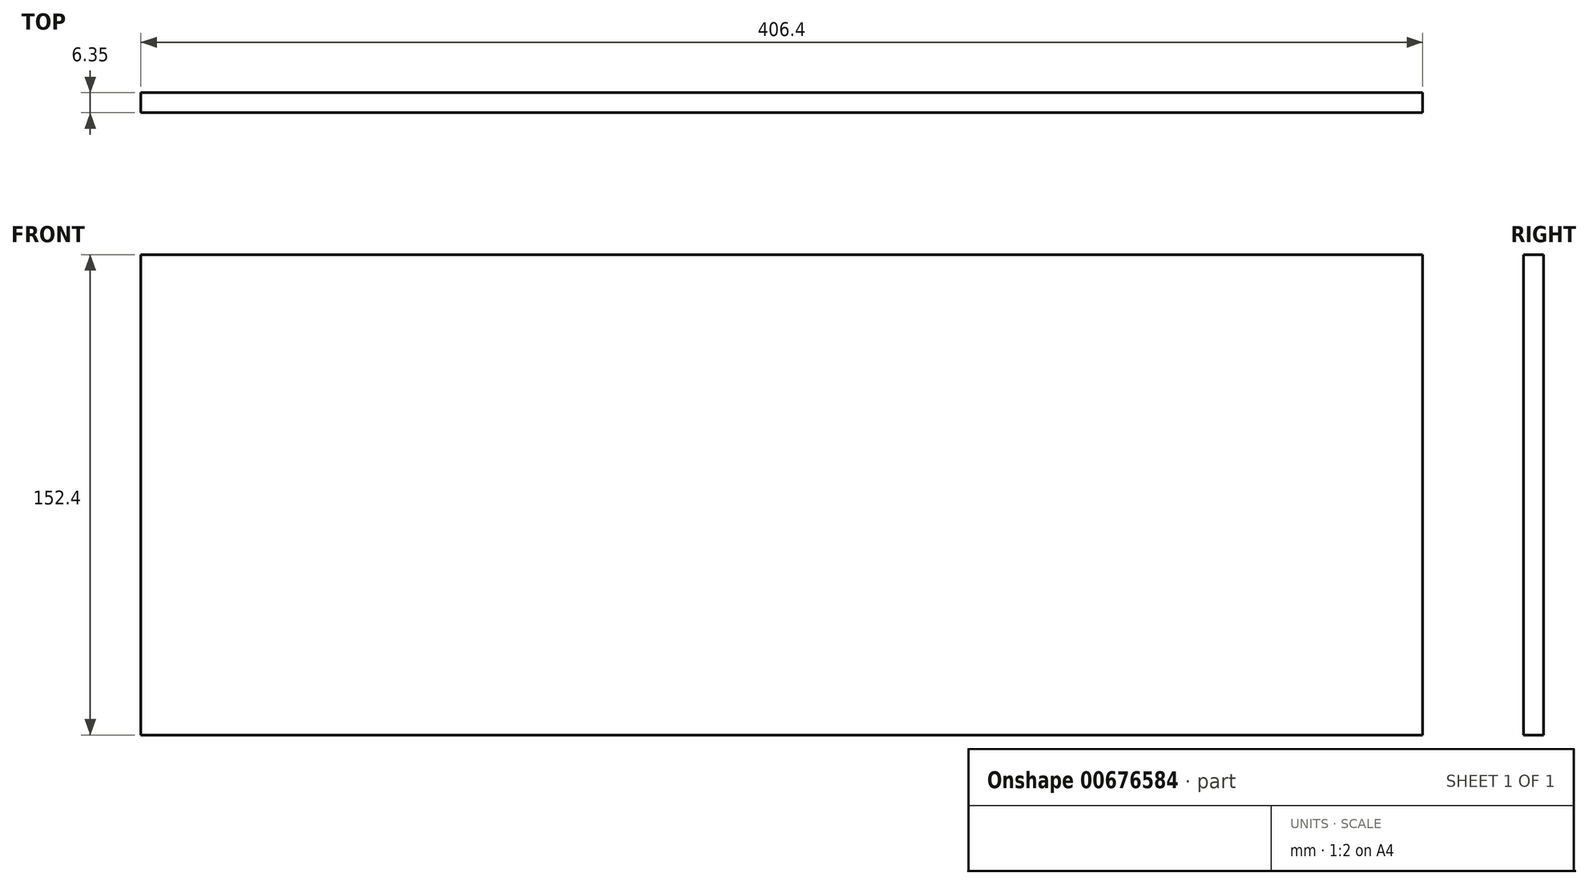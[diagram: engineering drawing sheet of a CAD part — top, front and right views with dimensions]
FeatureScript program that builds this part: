
annotation { "Feature Type Name" : "Feature", "Feature Type Description" : "" }
export const myFeature = defineFeature(function(context is Context, id is Id, definition is map)
    precondition{}
    {
        {
            var Q0;
            Q0=qCreatedBy(makeId("Front.planeOp"),FACE);
            var sketch = newSketch(context, id + "F0", { "sketchPlane" : qUnion([Q0])});
            skLineSegment(sketch, "E0.bottom", {"start": v(203.2, -76.2) * mm, "end": v(-203.2, -76.2) * mm});
            skLineSegment(sketch, "E0.top", {"start": v(203.2, 76.2) * mm, "end": v(-203.2, 76.2) * mm});
            skLineSegment(sketch, "E0.left", {"start": v(203.2, -76.2) * mm, "end": v(203.2, 76.2) * mm});
            skLineSegment(sketch, "E0.right", {"start": v(-203.2, -76.2) * mm, "end": v(-203.2, 76.2) * mm});
            skPoint(sketch, "E0.middle", {"position": v(0, 0) * mm});
            skSolve(sketch);
        }
        {
            var Q0;
            Q0 = qSketchRegion(id + "F0", true);
            extrude(context, id + "F1", {"entities" : qUnion([Q0]), "depth" : 6.35 * mm, "offsetDistance" : 25.4 * mm});
        }
    });
